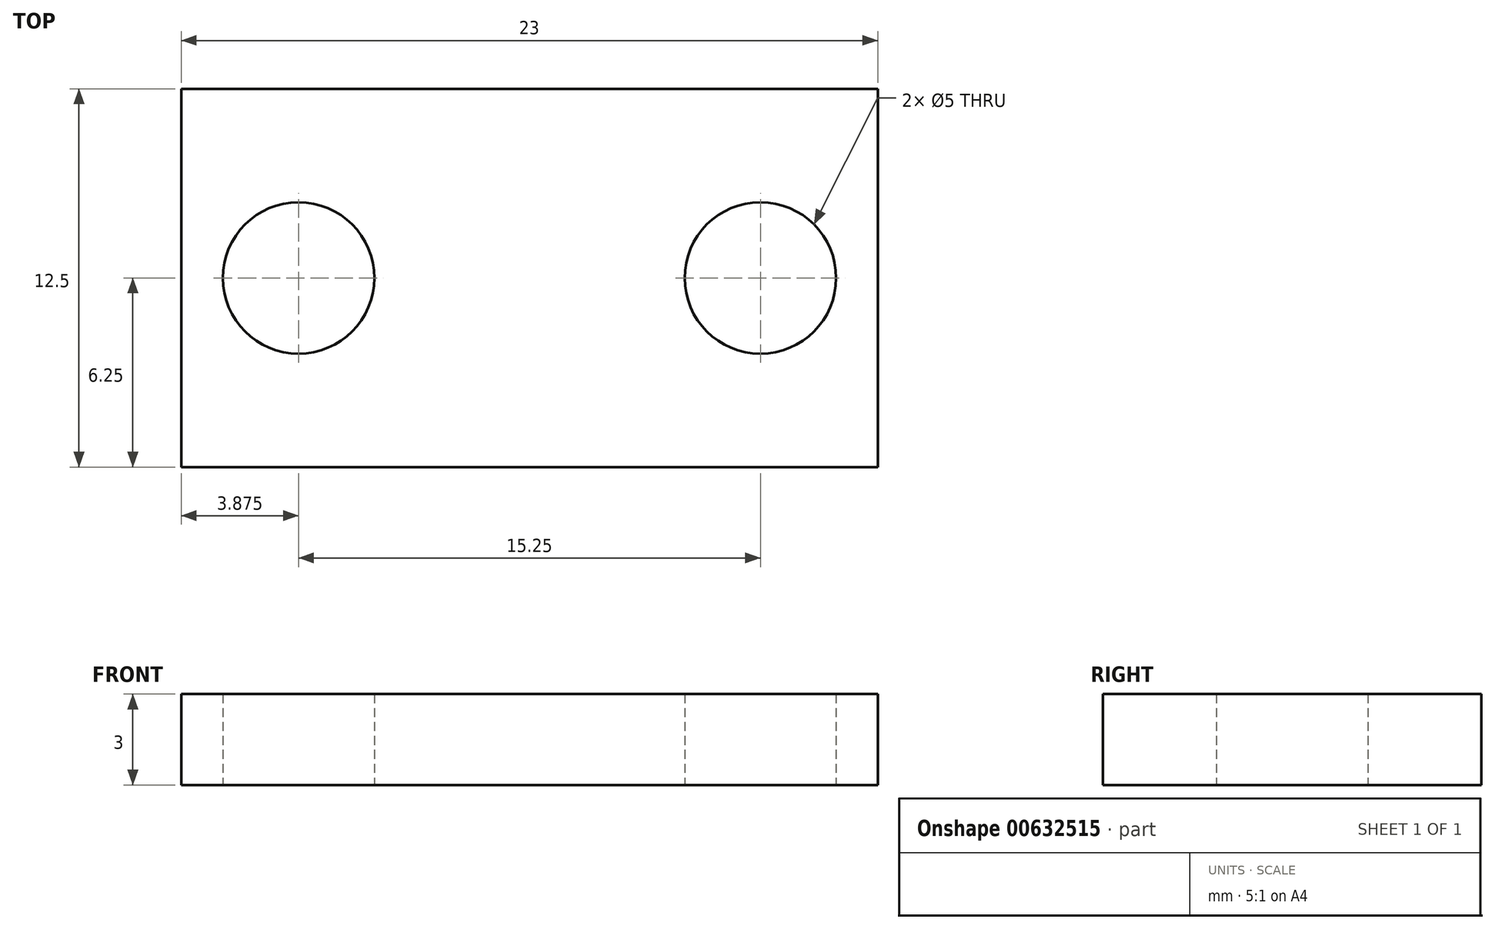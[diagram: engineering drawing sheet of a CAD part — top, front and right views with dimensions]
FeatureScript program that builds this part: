
annotation { "Feature Type Name" : "Feature", "Feature Type Description" : "" }
export const myFeature = defineFeature(function(context is Context, id is Id, definition is map)
    precondition{}
    {
        {
            var Q0;
            Q0=qCreatedBy(makeId("Top.planeOp"),FACE);
            var sketch = newSketch(context, id + "F0", { "sketchPlane" : qUnion([Q0])});
            skLineSegment(sketch, "E0.bottom", {"start": v(11.5, 6.25) * mm, "end": v(-11.5, 6.25) * mm});
            skLineSegment(sketch, "E0.top", {"start": v(11.5, -6.25) * mm, "end": v(-11.5, -6.25) * mm});
            skLineSegment(sketch, "E0.left", {"start": v(11.5, 6.25) * mm, "end": v(11.5, -6.25) * mm});
            skLineSegment(sketch, "E0.right", {"start": v(-11.5, 6.25) * mm, "end": v(-11.5, -6.25) * mm});
            skPoint(sketch, "E0.middle", {"position": v(0, 0) * mm});
            skLineSegment(sketch, "E1", {"start": v(-14.02, 0) * mm, "end": v(15.09, 0) * mm, "construction": true});
            skPoint(sketch, "E1.endSnap0", {"position": v(-11.5, 0) * mm});
            skCircle(sketch, "E2", {"center": v(-7.62, 0) * mm, "radius": 2.5 * mm});
            skCircle(sketch, "E3", {"center": v(7.63, 0) * mm, "radius": 2.5 * mm});
            skLineSegment(sketch, "E4", {"start": v(-7.62, 4.7) * mm, "end": v(-7.62, -5.18) * mm, "construction": true});
            skLineSegment(sketch, "E5", {"start": v(7.62, 4.79) * mm, "end": v(7.63, -4.86) * mm, "construction": true});
            skLineSegment(sketch, "E6", {"start": v(0, 7.11) * mm, "end": v(0, -7.6) * mm, "construction": true});
            skSolve(sketch);
        }
        {
            var Q0;
            Q0=makeQuery(id+"F0.imprint","IMPRINT",FACE,{"disambiguationData":[TD([[makeQuery(id+"F0.imprint","IMPRINT",EDGE,{"derivedFrom":sQuery(id+"F0.wireOp",EDGE,"E0.bottom")}),1.0]])]});
            extrude(context, id + "F1", {"entities" : qUnion([Q0]), "depth" : 3 * mm, "offsetDistance" : 25 * mm});
        }
    });
